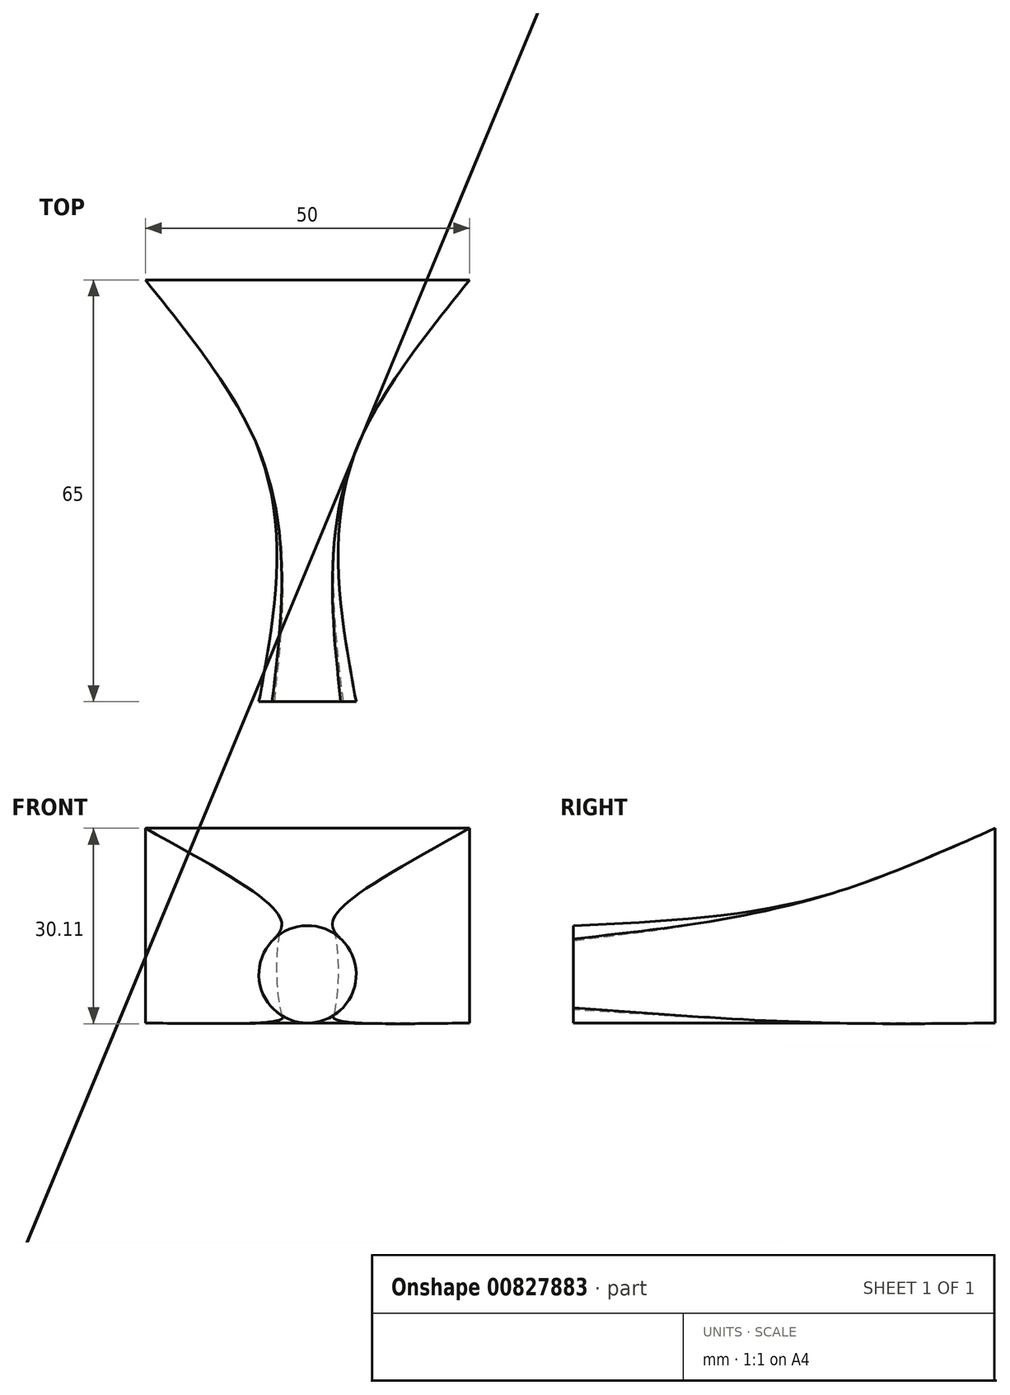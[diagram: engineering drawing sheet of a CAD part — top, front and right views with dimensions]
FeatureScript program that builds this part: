
annotation { "Feature Type Name" : "Feature", "Feature Type Description" : "" }
export const myFeature = defineFeature(function(context is Context, id is Id, definition is map)
    precondition{}
    {
        {
            var Q0;
            Q0=qCreatedBy(makeId("Front.planeOp"),FACE);
            var sketch = newSketch(context, id + "F0", { "sketchPlane" : qUnion([Q0])});
            skLineSegment(sketch, "E0.bottom", {"start": v(25, 0) * mm, "end": v(-25, 0) * mm});
            skLineSegment(sketch, "E0.top", {"start": v(25, 30) * mm, "end": v(-25, 30) * mm});
            skLineSegment(sketch, "E0.left", {"start": v(25, 0) * mm, "end": v(25, 30) * mm});
            skLineSegment(sketch, "E0.right", {"start": v(-25, 0) * mm, "end": v(-25, 30) * mm});
            skPoint(sketch, "E0.middle", {"position": v(0, 15) * mm});
            skSolve(sketch);
        }
        {
            var Q0;
            Q0=qCreatedBy(makeId("Front.planeOp"),FACE);
            cPlane(context, id + "F1", {"entities" : qUnion([Q0]), "cplaneType" : CPlaneType.OFFSET, "offset" : 25 * mm, "width" : 150 * mm, "height" : 150 * mm});
        }
        {
            var Q0;
            Q0=qCreatedBy(id+"F1.planeOp",FACE);
            var sketch = newSketch(context, id + "F2", { "sketchPlane" : qUnion([Q0])});
            skLineSegment(sketch, "E1.bottom", {"start": v(8, 0) * mm, "end": v(-8, 0) * mm});
            skLineSegment(sketch, "E1.top", {"start": v(8, 20) * mm, "end": v(-8, 20) * mm});
            skLineSegment(sketch, "E1.left", {"start": v(8, 0) * mm, "end": v(8, 20) * mm});
            skLineSegment(sketch, "E1.right", {"start": v(-8, 0) * mm, "end": v(-8, 20) * mm});
            skPoint(sketch, "E1.middle", {"position": v(0, 10) * mm});
            skSolve(sketch);
        }
        {
            var Q0;
            Q0=qCreatedBy(id+"F1.planeOp",FACE);
            cPlane(context, id + "F3", {"entities" : qUnion([Q0]), "cplaneType" : CPlaneType.OFFSET, "offset" : 40 * mm, "width" : 150 * mm, "height" : 150 * mm});
        }
        {
            var Q0;
            Q0=qCreatedBy(id+"F3.planeOp",FACE);
            var sketch = newSketch(context, id + "F4", { "sketchPlane" : qUnion([Q0])});
            skCircle(sketch, "E2", {"center": v(0, 7.5) * mm, "radius": 7.5 * mm});
            skSolve(sketch);
        }
        {
            var Q0;
            Q0=makeQuery(id+"F0.imprint","IMPRINT",FACE,{"disambiguationData":[TD([[makeQuery(id+"F0.imprint","IMPRINT",EDGE,{"derivedFrom":sQuery(id+"F0.wireOp",EDGE,"E0.bottom")}),-1.0]])]});
            var Q1;
            Q1 = qSketchRegion(id + "F2", true);
            var Q2;
            Q2 = qSketchRegion(id + "F4", true);
            loft(context, id + "F5", {"sheetProfilesArray" : [{ "sheetProfileEntities" : qUnion([Q0]) }, { "sheetProfileEntities" : qUnion([Q1]) }, { "sheetProfileEntities" : qUnion([Q2]) }]});
        }
    });
